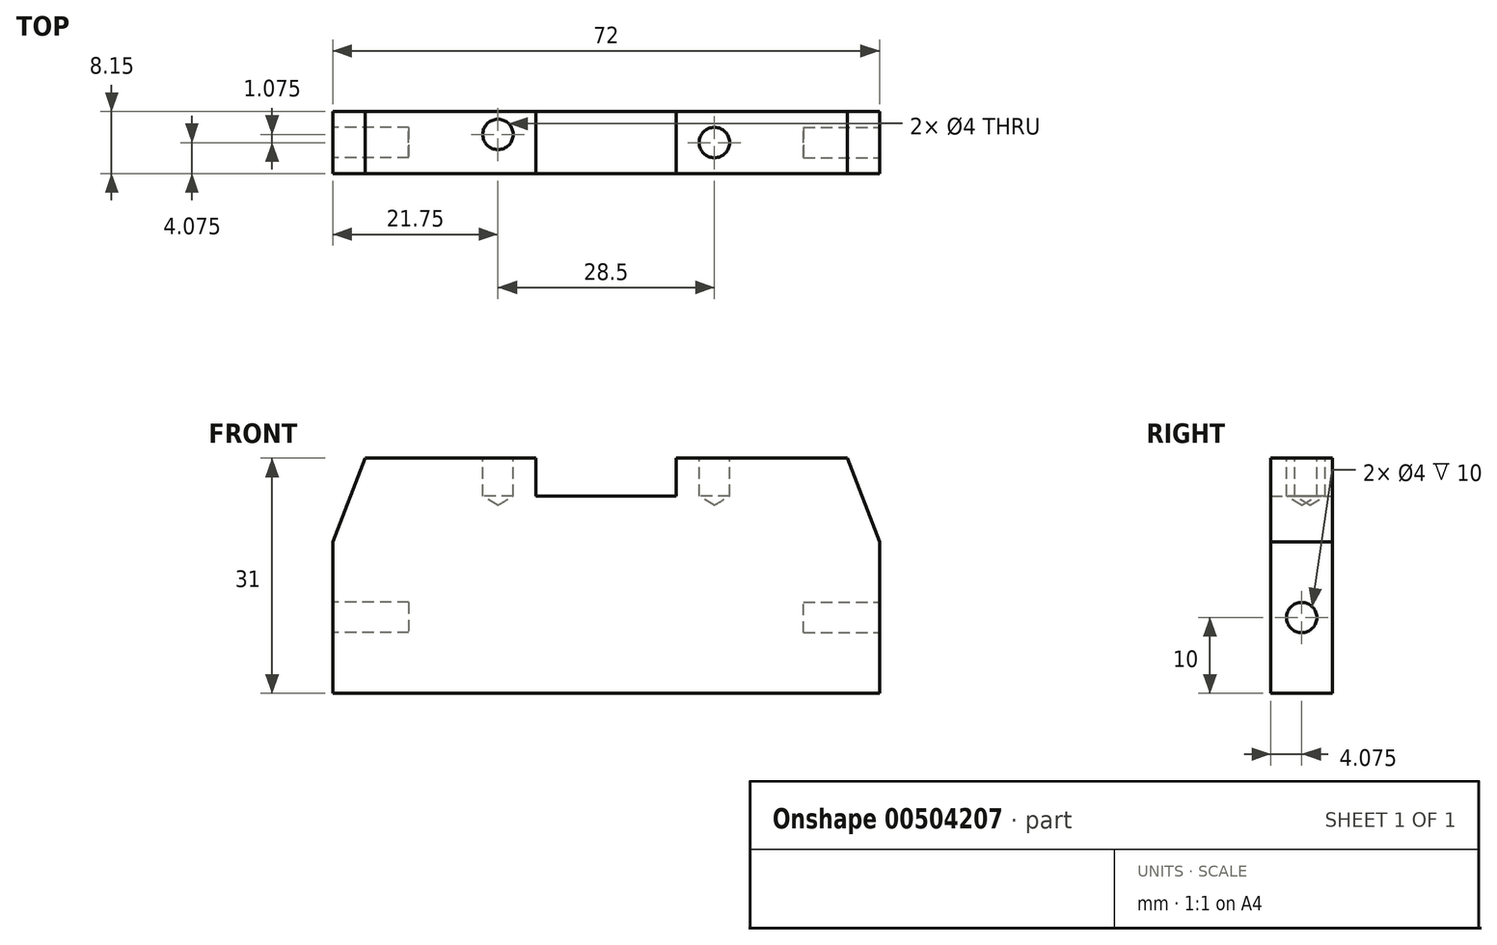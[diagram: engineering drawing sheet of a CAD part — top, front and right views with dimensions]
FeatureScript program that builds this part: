
annotation { "Feature Type Name" : "Feature", "Feature Type Description" : "" }
export const myFeature = defineFeature(function(context is Context, id is Id, definition is map)
    precondition{}
    {
        {
            var Q0;
            Q0=qCreatedBy(makeId("Front.planeOp"),FACE);
            var sketch = newSketch(context, id + "F0", { "sketchPlane" : qUnion([Q0])});
            skLineSegment(sketch, "E0", {"start": v(0, 0) * mm, "end": v(72, 0) * mm});
            skLineSegment(sketch, "E1", {"start": v(72, 0) * mm, "end": v(72, 20) * mm});
            skLineSegment(sketch, "E2", {"start": v(72, 20) * mm, "end": v(67.75, 31) * mm});
            skLineSegment(sketch, "E3", {"start": v(67.75, 31) * mm, "end": v(45.25, 31) * mm});
            skLineSegment(sketch, "E4", {"start": v(45.25, 31) * mm, "end": v(45.25, 26) * mm});
            skLineSegment(sketch, "E5", {"start": v(45.25, 26) * mm, "end": v(26.75, 26) * mm});
            skLineSegment(sketch, "E6", {"start": v(26.75, 26) * mm, "end": v(26.75, 31) * mm});
            skLineSegment(sketch, "E7", {"start": v(26.75, 31) * mm, "end": v(4.25, 31) * mm});
            skLineSegment(sketch, "E8", {"start": v(4.25, 31) * mm, "end": v(0, 20) * mm});
            skLineSegment(sketch, "E9", {"start": v(0, 20) * mm, "end": v(0, 0) * mm});
            skLineSegment(sketch, "E10", {"start": v(36, 0) * mm, "end": v(36, 47.24) * mm, "construction": true});
            skSolve(sketch);
        }
        {
            var Q0;
            Q0=makeQuery(id+"F0.imprint","IMPRINT",FACE,{"disambiguationData":[TD([[makeQuery(id+"F0.imprint","IMPRINT",EDGE,{"derivedFrom":sQuery(id+"F0.wireOp",EDGE,"E0")}),1.0]])]});
            extrude(context, id + "F1", {"entities" : qUnion([Q0]), "offsetDistance" : 25 * mm, "depth" : 8.15 * mm});
        }
        {
            var Q0;
            Q0=makeQuery(id+"F1.opExtrude","SWEPT_FACE",FACE,{"disambiguationData":[OSD([sQuery(id+"F0.wireOp",EDGE,"E3")])]});
            var sketch = newSketch(context, id + "F2", { "sketchPlane" : qUnion([Q0])});
            skCircle(sketch, "E11", {"center": v(50.25, -4.07) * mm, "radius": 1.88 * mm});
            skPoint(sketch, "E11.centerSnap0", {"position": v(45.25, -4.07) * mm});
            skCircle(sketch, "E12", {"center": v(21.75, -3) * mm, "radius": 1.77 * mm});
            skSolve(sketch);
        }
        {
            var Q0;
            Q0=sQuery(id+"F2.wireOp",VERTEX,"E12.center");
            var Q1;
            Q1=sQuery(id+"F2.wireOp",VERTEX,"E11.center");
            var Q2;
            Q2=makeQuery(id+"F1.opExtrude","SWEPT_BODY",BODY,{"disambiguationData":[OSD([sQuery(id+"F0.wireOp",EDGE,"E0"),sQuery(id+"F0.wireOp",EDGE,"E1"),sQuery(id+"F0.wireOp",EDGE,"E2"),sQuery(id+"F0.wireOp",EDGE,"E3"),sQuery(id+"F0.wireOp",EDGE,"E4"),sQuery(id+"F0.wireOp",EDGE,"E5"),sQuery(id+"F0.wireOp",EDGE,"E6"),sQuery(id+"F0.wireOp",EDGE,"E7"),sQuery(id+"F0.wireOp",EDGE,"E8"),sQuery(id+"F0.wireOp",EDGE,"E9")])]});
            hole(context, id + "F3", {"style" : HoleStyle.SIMPLE, "endStyle" : HoleEndStyle.BLIND, "holeDiameter" : 4 * mm, "holeDepth" : 5 * mm, "isTappedThrough" : true, "tappedDepth" : 12 * mm, "tapClearance" : 3, "locations" : qUnion([Q0, Q1]), "scope" : qUnion([Q2])});
        }
        {
            var Q0;
            Q0=makeQuery(id+"F1.opExtrude","SWEPT_FACE",FACE,{"disambiguationData":[OSD([sQuery(id+"F0.wireOp",EDGE,"E1")])]});
            var sketch = newSketch(context, id + "F4", { "sketchPlane" : qUnion([Q0])});
            skCircle(sketch, "E13", {"center": v(-4.08, 10) * mm, "radius": 2 * mm});
            skPoint(sketch, "E13.centerSnap0", {"position": v(0, 10) * mm});
            skPoint(sketch, "E13.centerSnap1", {"position": v(-4.08, 0) * mm});
            skSolve(sketch);
        }
        {
            var Q0;
            Q0=makeQuery(id+"F4.imprint","IMPRINT",FACE,{"disambiguationData":[TD([[makeQuery(id+"F4.imprint","IMPRINT",EDGE,{"derivedFrom":sQuery(id+"F4.wireOp",EDGE,"E13")}),1.0]])]});
            extrude(context, id + "F5", {"entities" : qUnion([Q0]), "operationType" : NewBodyOperationType.REMOVE, "oppositeDirection" : true, "depth" : 10 * mm});
        }
        {
            var Q0;
            Q0=makeQuery(id+"F1.opExtrude","SWEPT_FACE",FACE,{"disambiguationData":[OSD([sQuery(id+"F0.wireOp",EDGE,"E9")])]});
            var sketch = newSketch(context, id + "F6", { "sketchPlane" : qUnion([Q0])});
            skCircle(sketch, "E14", {"center": v(4.07, 10) * mm, "radius": 2 * mm});
            skPoint(sketch, "E14.centerSnap0", {"position": v(8.15, 10) * mm});
            skPoint(sketch, "E14.centerSnap1", {"position": v(4.08, 0) * mm});
            skSolve(sketch);
        }
        {
            var Q0;
            Q0=makeQuery(id+"F6.imprint","IMPRINT",FACE,{"disambiguationData":[TD([[makeQuery(id+"F6.imprint","IMPRINT",EDGE,{"derivedFrom":sQuery(id+"F6.wireOp",EDGE,"E14")}),1.0]])]});
            extrude(context, id + "F7", {"entities" : qUnion([Q0]), "operationType" : NewBodyOperationType.REMOVE, "oppositeDirection" : true, "depth" : 10 * mm});
        }
    });
